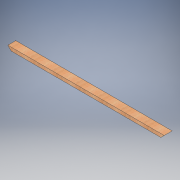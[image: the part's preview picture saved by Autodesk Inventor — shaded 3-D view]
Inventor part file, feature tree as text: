
AUTODESK INVENTOR PART (.ipt)
format: ipt  version: 2016 (Build 200138000, 138)  size: 98,816 bytes
history: native  units: in
note: dims shown in document units (in); Inventor stores cm internally (conversion verified against a paired STEP export)
features: extrude x1, sketch x1
ambient origin geometry x8: Origin, YZ Plane, XZ Plane, XY Plane, X Axis, Y Axis, Z Axis, Center Point
bodies: Body1 (feature_tree)
feature tree (2):
  extrude  "Extrusion2"  TaperAngle=135.0deg  [1 undecoded]
  sketch  "Sketch2"  dims[d10=45.0deg d11=135.0deg d12=3.5in d13=0.0in d14=69.0in d15=1.5in]
note: 1 required parameter value undecoded (feature->parameter linkage not recoverable at this tier; creation-order binding heuristic only, values carry confidence <= 0.55)
